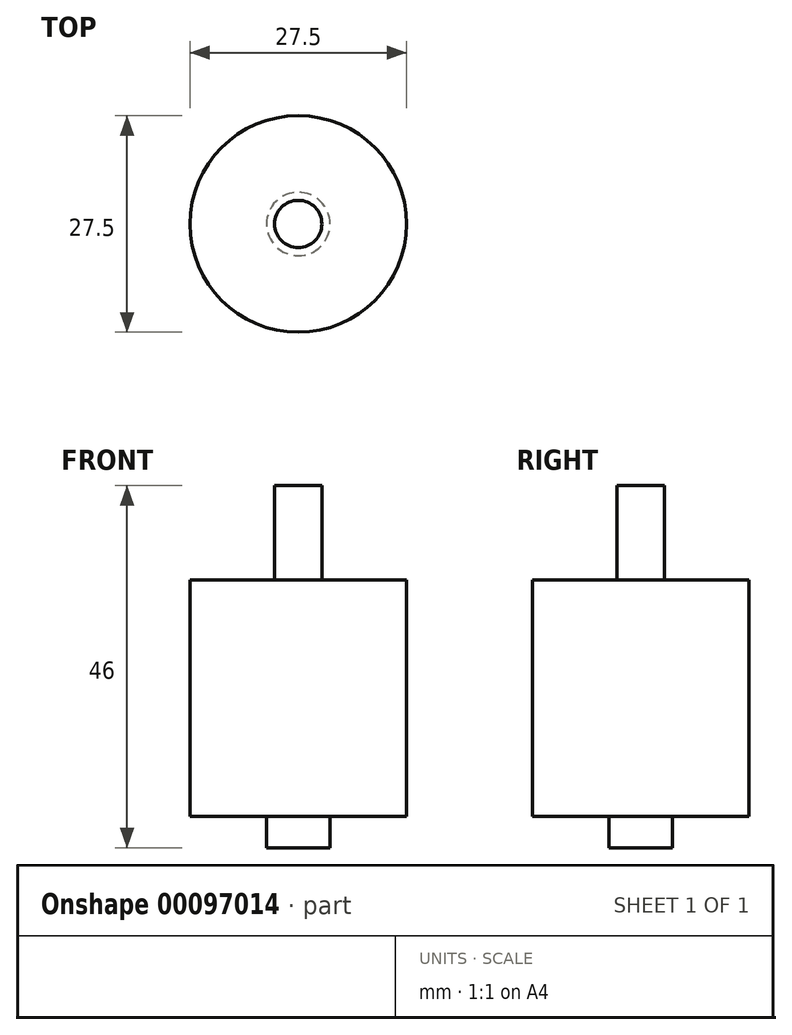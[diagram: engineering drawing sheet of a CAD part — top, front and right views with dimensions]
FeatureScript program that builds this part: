
annotation { "Feature Type Name" : "Feature", "Feature Type Description" : "" }
export const myFeature = defineFeature(function(context is Context, id is Id, definition is map)
    precondition{}
    {
        {
            var Q0;
            Q0=qCreatedBy(makeId("Top.planeOp"),FACE);
            var sketch = newSketch(context, id + "F0", { "sketchPlane" : qUnion([Q0])});
            skCircle(sketch, "E0", {"center": v(0, 0) * mm, "radius": 4.03 * mm});
            skSolve(sketch);
        }
        {
            var Q0;
            Q0 = qSketchRegion(id + "F0", true);
            var Q1;
            Q1 = qSketchRegion(id + "F2", true);
            extrude(context, id + "F1", {"entities" : qUnion([Q0, Q1]), "depth" : 4 * mm});
        }
        {
            var Q0;
            Q0=makeQuery(id+"F1.opExtrude","CAP_FACE",FACE,{"disambiguationData":[OSD([sQuery(id+"F0.wireOp",EDGE,"E0")])],"isStart":false});
            var sketch = newSketch(context, id + "F2", { "sketchPlane" : qUnion([Q0])});
            skCircle(sketch, "E1", {"center": v(0, 0) * mm, "radius": 13.75 * mm});
            skSolve(sketch);
        }
        {
            var Q0;
            Q0 = qSketchRegion(id + "F2", true);
            extrude(context, id + "F3", {"entities" : qUnion([Q0]), "operationType" : NewBodyOperationType.ADD, "depth" : 30 * mm});
        }
        {
            var Q0;
            Q0=makeQuery(id+"F3.opExtrude","CAP_FACE",FACE,{"disambiguationData":[OSD([sQuery(id+"F2.wireOp",EDGE,"E1")])],"isStart":false});
            var sketch = newSketch(context, id + "F4", { "sketchPlane" : qUnion([Q0])});
            skCircle(sketch, "E2", {"center": v(0, 0) * mm, "radius": 3 * mm});
            skSolve(sketch);
        }
        {
            var Q0;
            Q0 = qSketchRegion(id + "F4", true);
            extrude(context, id + "F5", {"entities" : qUnion([Q0]), "operationType" : NewBodyOperationType.ADD, "depth" : 12 * mm});
        }
    });
